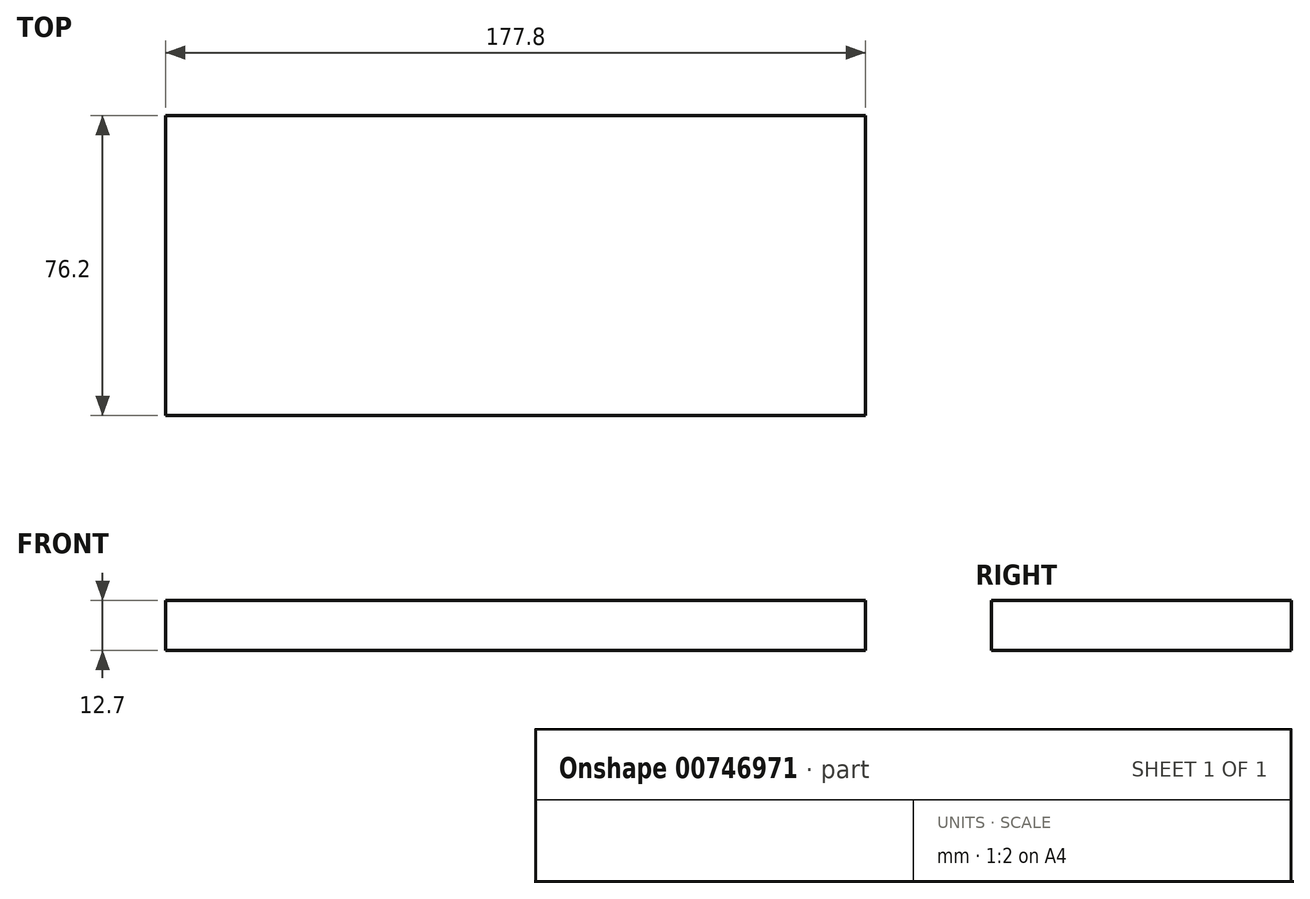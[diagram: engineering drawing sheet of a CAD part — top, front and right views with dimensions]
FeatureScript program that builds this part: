
annotation { "Feature Type Name" : "Feature", "Feature Type Description" : "" }
export const myFeature = defineFeature(function(context is Context, id is Id, definition is map)
    precondition{}
    {
        {
            var Q0;
            Q0=qCreatedBy(makeId("Top.planeOp"),FACE);
            var sketch = newSketch(context, id + "F0", { "sketchPlane" : qUnion([Q0])});
            skLineSegment(sketch, "E0.bottom", {"start": v(-83.57, 49.23) * mm, "end": v(94.23, 49.23) * mm});
            skLineSegment(sketch, "E0.top", {"start": v(-83.57, -26.97) * mm, "end": v(94.23, -26.97) * mm});
            skLineSegment(sketch, "E0.left", {"start": v(-83.57, 49.23) * mm, "end": v(-83.57, -26.97) * mm});
            skLineSegment(sketch, "E0.right", {"start": v(94.23, 49.23) * mm, "end": v(94.23, -26.97) * mm});
            skSolve(sketch);
        }
        {
            var Q0;
            Q0 = qSketchRegion(id + "F0", true);
            extrude(context, id + "F1", {"entities" : qUnion([Q0]), "depth" : 12.7 * mm, "offsetDistance" : 25.4 * mm});
        }
    });
